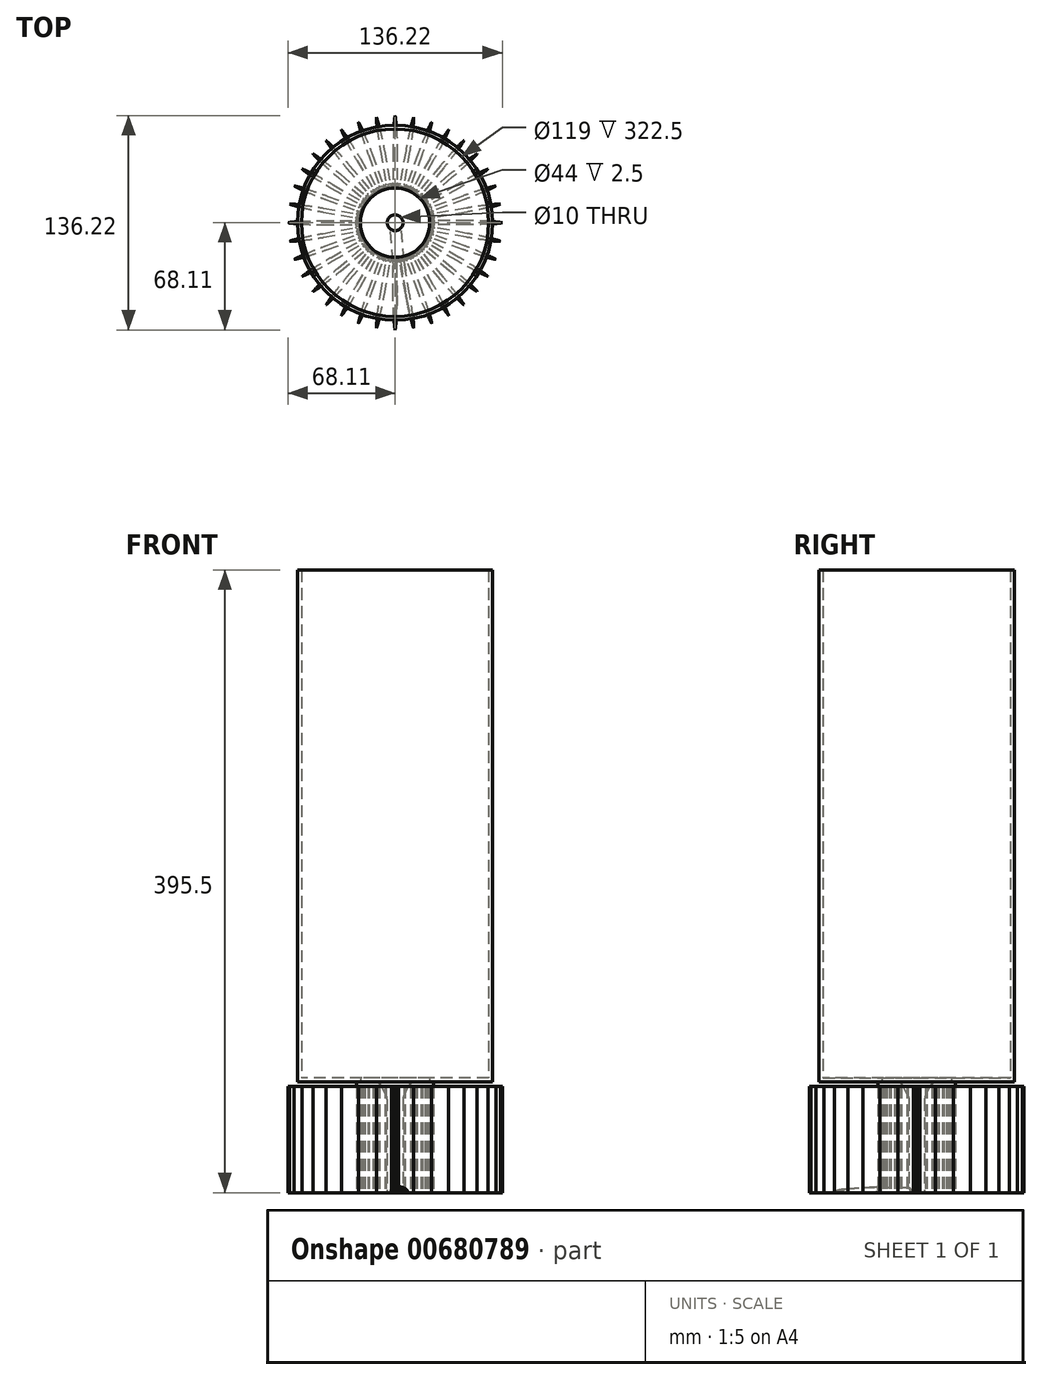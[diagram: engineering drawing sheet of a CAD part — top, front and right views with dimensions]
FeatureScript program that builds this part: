
annotation { "Feature Type Name" : "Feature", "Feature Type Description" : "" }
export const myFeature = defineFeature(function(context is Context, id is Id, definition is map)
    precondition{}
    {
        {
            var Q0;
            Q0=qCreatedBy(makeId("Top.planeOp"),FACE);
            var sketch = newSketch(context, id + "F0", { "sketchPlane" : qUnion([Q0])});
            skCircle(sketch, "E0", {"center": v(0, 0) * mm, "radius": 62 * mm, "construction": true});
            skCircle(sketch, "E1", {"center": v(0, 0) * mm, "radius": 22 * mm, "construction": true});
            skCircle(sketch, "E2", {"center": v(0, 0) * mm, "radius": 24.5 * mm, "construction": true});
            skSolve(sketch);
        }
        {
            var Q0;
            Q0=qCreatedBy(makeId("Top.planeOp"),FACE);
            var sketch = newSketch(context, id + "F1", { "sketchPlane" : qUnion([Q0])});
            skCircle(sketch, "E3", {"center": v(0, 0) * mm, "radius": 24.5 * mm});
            skSolve(sketch);
        }
        {
            var Q0;
            Q0=makeQuery(id+"F1.imprint","IMPRINT",FACE,{"disambiguationData":[TD([[makeQuery(id+"F1.imprint","IMPRINT",EDGE,{"derivedFrom":sQuery(id+"F1.wireOp",EDGE,"E3")}),1.0]])]});
            extrude(context, id + "F2", {"entities" : qUnion([Q0]), "depth" : 70.5 * mm, "offsetDistance" : 25 * mm});
        }
        {
            var Q0;
            Q0=makeQuery(id+"F2.opExtrude","CAP_FACE",FACE,{"disambiguationData":[OSD([sQuery(id+"F1.wireOp",EDGE,"E3")])],"isStart":false});
            var sketch = newSketch(context, id + "F3", { "sketchPlane" : qUnion([Q0])});
            skCircle(sketch, "E4", {"center": v(0, 0) * mm, "radius": 22 * mm});
            skSolve(sketch);
        }
        {
            var Q0;
            Q0=makeQuery(id+"F3.imprint","IMPRINT",FACE,{"disambiguationData":[TD([[makeQuery(id+"F3.imprint","IMPRINT",EDGE,{"derivedFrom":sQuery(id+"F3.wireOp",EDGE,"E4")}),-1.0]])]});
            extrude(context, id + "F4", {"entities" : qUnion([Q0]), "operationType" : NewBodyOperationType.REMOVE, "oppositeDirection" : true, "depth" : 3 * mm, "offsetDistance" : 25 * mm});
        }
        {
            var Q0;
            Q0=qCreatedBy(makeId("Top.planeOp"),FACE);
            var sketch = newSketch(context, id + "F5", { "sketchPlane" : qUnion([Q0])});
            skLineSegment(sketch, "E5", {"start": v(0, 24.5) * mm, "end": v(0, 62) * mm, "construction": true});
            skLineSegment(sketch, "E6.1.0", {"start": v(4.37, 24.1) * mm, "end": v(11.07, 61) * mm, "construction": true});
            skLineSegment(sketch, "E6.2.0", {"start": v(8.6, 22.94) * mm, "end": v(21.79, 58.05) * mm, "construction": true});
            skLineSegment(sketch, "E6.3.0", {"start": v(12.57, 21.03) * mm, "end": v(31.8, 53.22) * mm, "construction": true});
            skLineSegment(sketch, "E6.4.0", {"start": v(16.12, 18.45) * mm, "end": v(40.8, 46.7) * mm, "construction": true});
            skLineSegment(sketch, "E6.5.0", {"start": v(19.15, 15.28) * mm, "end": v(48.47, 38.66) * mm, "construction": true});
            skLineSegment(sketch, "E6.6.0", {"start": v(21.57, 11.6) * mm, "end": v(54.6, 29.38) * mm, "construction": true});
            skLineSegment(sketch, "E6.7.0", {"start": v(23.3, 7.57) * mm, "end": v(58.97, 19.16) * mm, "construction": true});
            skLineSegment(sketch, "E6.8.0", {"start": v(24.28, 3.29) * mm, "end": v(61.44, 8.32) * mm, "construction": true});
            skLineSegment(sketch, "E6.9.0", {"start": v(24.48, -1.1) * mm, "end": v(61.94, -2.78) * mm, "construction": true});
            skLineSegment(sketch, "E6.10.0", {"start": v(23.89, -5.45) * mm, "end": v(60.45, -13.8) * mm, "construction": true});
            skLineSegment(sketch, "E6.11.0", {"start": v(22.53, -9.63) * mm, "end": v(57.01, -24.37) * mm, "construction": true});
            skLineSegment(sketch, "E6.12.0", {"start": v(20.45, -13.5) * mm, "end": v(51.74, -34.16) * mm, "construction": true});
            skLineSegment(sketch, "E6.13.0", {"start": v(17.7, -16.93) * mm, "end": v(44.81, -42.85) * mm, "construction": true});
            skLineSegment(sketch, "E6.14.0", {"start": v(14.4, -19.82) * mm, "end": v(36.44, -50.16) * mm, "construction": true});
            skLineSegment(sketch, "E6.15.0", {"start": v(10.63, -22.07) * mm, "end": v(26.9, -55.86) * mm, "construction": true});
            skLineSegment(sketch, "E6.16.0", {"start": v(6.52, -23.62) * mm, "end": v(16.5, -59.77) * mm, "construction": true});
            skLineSegment(sketch, "E6.17.0", {"start": v(2.2, -24.4) * mm, "end": v(5.56, -61.75) * mm, "construction": true});
            skLineSegment(sketch, "E6.18.0", {"start": v(-2.2, -24.4) * mm, "end": v(-5.56, -61.75) * mm, "construction": true});
            skLineSegment(sketch, "E6.19.0", {"start": v(-6.52, -23.62) * mm, "end": v(-16.5, -59.77) * mm, "construction": true});
            skLineSegment(sketch, "E6.20.0", {"start": v(-10.63, -22.07) * mm, "end": v(-26.9, -55.86) * mm, "construction": true});
            skLineSegment(sketch, "E6.21.0", {"start": v(-14.4, -19.82) * mm, "end": v(-36.44, -50.16) * mm, "construction": true});
            skLineSegment(sketch, "E6.22.0", {"start": v(-17.7, -16.93) * mm, "end": v(-44.81, -42.85) * mm, "construction": true});
            skLineSegment(sketch, "E6.23.0", {"start": v(-20.45, -13.5) * mm, "end": v(-51.74, -34.16) * mm, "construction": true});
            skLineSegment(sketch, "E6.24.0", {"start": v(-22.53, -9.63) * mm, "end": v(-57.01, -24.37) * mm, "construction": true});
            skLineSegment(sketch, "E6.25.0", {"start": v(-23.89, -5.45) * mm, "end": v(-60.45, -13.8) * mm, "construction": true});
            skLineSegment(sketch, "E6.26.0", {"start": v(-24.48, -1.1) * mm, "end": v(-61.94, -2.78) * mm, "construction": true});
            skLineSegment(sketch, "E6.27.0", {"start": v(-24.28, 3.29) * mm, "end": v(-61.44, 8.32) * mm, "construction": true});
            skLineSegment(sketch, "E6.28.0", {"start": v(-23.3, 7.57) * mm, "end": v(-58.97, 19.16) * mm, "construction": true});
            skLineSegment(sketch, "E6.29.0", {"start": v(-21.57, 11.6) * mm, "end": v(-54.6, 29.38) * mm, "construction": true});
            skLineSegment(sketch, "E6.30.0", {"start": v(-19.15, 15.28) * mm, "end": v(-48.47, 38.66) * mm, "construction": true});
            skLineSegment(sketch, "E6.31.0", {"start": v(-16.12, 18.45) * mm, "end": v(-40.8, 46.7) * mm, "construction": true});
            skLineSegment(sketch, "E6.32.0", {"start": v(-12.57, 21.03) * mm, "end": v(-31.8, 53.22) * mm, "construction": true});
            skLineSegment(sketch, "E6.33.0", {"start": v(-8.6, 22.94) * mm, "end": v(-21.79, 58.05) * mm, "construction": true});
            skLineSegment(sketch, "E6.34.0", {"start": v(-4.37, 24.1) * mm, "end": v(-11.07, 61) * mm, "construction": true});
            skPoint(sketch, "E6.center", {"position": v(0, 0) * mm});
            skLineSegment(sketch, "E6.anchor1", {"start": v(0, 0) * mm, "end": v(0, 24.5) * mm, "construction": true});
            skLineSegment(sketch, "E6.anchor2", {"start": v(0, 0) * mm, "end": v(0, 24.5) * mm, "construction": true});
            skSolve(sketch);
        }
        {
            var Q0;
            Q0=qCreatedBy(makeId("Top.planeOp"),FACE);
            var sketch = newSketch(context, id + "F6", { "sketchPlane" : qUnion([Q0])});
            skLineSegment(sketch, "E7.bottom", {"start": v(-1.24, 68.1) * mm, "end": v(1.24, 68.1) * mm, "construction": true});
            skLineSegment(sketch, "E7.left", {"start": v(-1.24, 68.1) * mm, "end": v(-1.24, 24.47) * mm, "construction": true});
            skPoint(sketch, "E7.middle", {"position": v(0, 46.29) * mm});
            skArc(sketch, "E8", {"start": v(1.24, 24.47) * mm, "mid": v(1.69, 24.44) * mm, "end": v(2.14, 24.4) * mm, "construction": true});
            skArc(sketch, "E9", {"start": v(-1.24, 24.47) * mm, "mid": v(-1.69, 24.44) * mm, "end": v(-2.14, 24.4) * mm, "construction": true});
            skLineSegment(sketch, "E10", {"start": v(-2.14, 24.4) * mm, "end": v(0, 0) * mm, "construction": true});
            skLineSegment(sketch, "E11", {"start": v(0, 0) * mm, "end": v(2.14, 24.4) * mm, "construction": true});
            skArc(sketch, "E12", {"start": v(-2.02, 23.1) * mm, "mid": v(0, 23.2) * mm, "end": v(2.02, 23.1) * mm, "construction": true});
            skFitSpline(sketch, "E13", {"points": [v(0, 68.1) * mm, v(-1.24, 46.29) * mm], "startDerivative": vector(-2.7, -15.81) * mm, "endDerivative": vector(0, -17.84) * mm});
            skFitSpline(sketch, "E14.MirrorCS", {"points": [v(0, 68.1) * mm, v(1.24, 46.29) * mm], "startDerivative": vector(2.7, -15.81) * mm, "endDerivative": vector(0, -17.84) * mm});
            skLineSegment(sketch, "E15", {"start": v(-1.24, 46.29) * mm, "end": v(-1.24, 25.38) * mm});
            skLineSegment(sketch, "E16", {"start": v(2.14, 24.4) * mm, "end": v(2.02, 23.1) * mm});
            skLineSegment(sketch, "E17", {"start": v(-2.14, 24.4) * mm, "end": v(-2.02, 23.1) * mm});
            skArc(sketch, "E18", {"start": v(-2.02, 23.1) * mm, "mid": v(0, 23.2) * mm, "end": v(2.02, 23.1) * mm});
            skLineSegment(sketch, "E19", {"start": v(-2.14, 24.4) * mm, "end": v(-2.14, 24.4) * mm});
            skArc(sketch, "E20", {"start": v(2.14, 24.4) * mm, "mid": v(1.69, 24.44) * mm, "end": v(1.24, 24.47) * mm});
            skPoint(sketch, "E21.visualSharp", {"position": v(-1.24, 24.47) * mm});
            skArc(sketch, "E21.filletArc", {"start": v(-2.14, 24.4) * mm, "mid": v(-1.5, 24.72) * mm, "end": v(-1.24, 25.38) * mm});
            skArc(sketch, "E22.MirrorCS", {"start": v(2.14, 24.4) * mm, "mid": v(1.5, 24.72) * mm, "end": v(1.24, 25.38) * mm});
            skLineSegment(sketch, "E23.MirrorCS", {"start": v(1.24, 68.1) * mm, "end": v(1.24, 24.47) * mm, "construction": true});
            skLineSegment(sketch, "E24", {"start": v(1.24, 46.29) * mm, "end": v(1.24, 25.38) * mm});
            skArc(sketch, "E25.filletArc", {"start": v(0.73, 61.3) * mm, "mid": v(0, 61.98) * mm, "end": v(-0.73, 61.3) * mm});
            skSolve(sketch);
        }
        {
            var Q0;
            Q0 = qSketchRegion(id + "F6", true);
            extrude(context, id + "F7", {"entities" : qUnion([Q0]), "depth" : 67.5 * mm, "offsetDistance" : 25 * mm});
        }
        {
            var Q0;
            Q0=qCreatedBy(makeId("Front.planeOp"),FACE);
            var sketch = newSketch(context, id + "F8", { "sketchPlane" : qUnion([Q0])});
            skLineSegment(sketch, "E26", {"start": v(0, 70.5) * mm, "end": v(0, 0) * mm, "construction": true});
            skSolve(sketch);
        }
        {
            var Q0;
            Q0=makeQuery(id+"F7.opExtrude","SWEPT_BODY",BODY,{"disambiguationData":[OSD([sQuery(id+"F6.wireOp",EDGE,"E13"),sQuery(id+"F6.wireOp",EDGE,"E14.MirrorCS"),sQuery(id+"F6.wireOp",EDGE,"E15"),sQuery(id+"F6.wireOp",EDGE,"E16"),sQuery(id+"F6.wireOp",EDGE,"E17"),sQuery(id+"F6.wireOp",EDGE,"E18"),sQuery(id+"F6.wireOp",EDGE,"E21.filletArc"),sQuery(id+"F6.wireOp",EDGE,"E22.MirrorCS"),sQuery(id+"F6.wireOp",EDGE,"E24")])]});
            var Q1;
            Q1=sQuery(id+"F8.wireOp",EDGE,"E26");
            circularPattern(context, id + "F9", {"entities" : qUnion([Q0]), "axis" : qUnion([Q1]), "angle" : 360 * degree, "instanceCount" : 36, "equalSpace" : true});
        }
        {
            var Q0;
            Q0=makeQuery(id+"F9.opPattern","COPY",FACE,{"derivedFrom":makeQuery(id+"F7.opExtrude","CAP_FACE",FACE,{"disambiguationData":[OSD([sQuery(id+"F6.wireOp",EDGE,"E13"),sQuery(id+"F6.wireOp",EDGE,"E14.MirrorCS"),sQuery(id+"F6.wireOp",EDGE,"E15"),sQuery(id+"F6.wireOp",EDGE,"E16"),sQuery(id+"F6.wireOp",EDGE,"E17"),sQuery(id+"F6.wireOp",EDGE,"E18"),sQuery(id+"F6.wireOp",EDGE,"E21.filletArc"),sQuery(id+"F6.wireOp",EDGE,"E22.MirrorCS"),sQuery(id+"F6.wireOp",EDGE,"E24")])],"isStart":false}),"instanceName":"19"});
            var sketch = newSketch(context, id + "F10", { "sketchPlane" : qUnion([Q0])});
            skCircle(sketch, "E27", {"center": v(0, 0) * mm, "radius": 62 * mm, "construction": true});
            skCircle(sketch, "E28", {"center": v(0, 0) * mm, "radius": 22 * mm});
            skCircle(sketch, "E29", {"center": v(0, 0) * mm, "radius": 24.5 * mm});
            skSolve(sketch);
        }
        {
            var Q0;
            Q0 = qSketchRegion(id + "F10", true);
            extrude(context, id + "F11", {"entities" : qUnion([Q0]), "depth" : 3 * mm, "offsetDistance" : 25 * mm});
        }
        {
            var Q0;
            Q0=makeQuery(id+"F11.opExtrude","CAP_FACE",FACE,{"disambiguationData":[OSD([sQuery(id+"F10.wireOp",EDGE,"E28"),sQuery(id+"F10.wireOp",EDGE,"E29")])],"isStart":false});
            var sketch = newSketch(context, id + "F12", { "sketchPlane" : qUnion([Q0])});
            skCircle(sketch, "E30", {"center": v(0, 0) * mm, "radius": 22 * mm});
            skCircle(sketch, "E31", {"center": v(0, 0) * mm, "radius": 62 * mm});
            skSolve(sketch);
        }
        {
            var Q0;
            Q0 = qSketchRegion(id + "F12", true);
            extrude(context, id + "F13", {"entities" : qUnion([Q0]), "operationType" : NewBodyOperationType.ADD, "depth" : 2.5 * mm, "offsetDistance" : 25 * mm});
        }
        {
            var Q0;
            Q0=makeQuery(id+"F13.opExtrude","CAP_FACE",FACE,{"disambiguationData":[OSD([sQuery(id+"F12.wireOp",EDGE,"E30"),sQuery(id+"F12.wireOp",EDGE,"E31")])],"isStart":false});
            var sketch = newSketch(context, id + "F14", { "sketchPlane" : qUnion([Q0])});
            skCircle(sketch, "E32", {"center": v(0, 0) * mm, "radius": 62 * mm});
            skCircle(sketch, "E33", {"center": v(0, 0) * mm, "radius": 59.5 * mm});
            skSolve(sketch);
        }
        {
            var Q0;
            Q0=makeQuery(id+"F14.imprint","IMPRINT",FACE,{"disambiguationData":[TD([[makeQuery(id+"F14.imprint","IMPRINT",EDGE,{"derivedFrom":sQuery(id+"F14.wireOp",EDGE,"E32")}),1.0]])]});
            extrude(context, id + "F15", {"entities" : qUnion([Q0]), "operationType" : NewBodyOperationType.ADD, "depth" : 25 * mm, "offsetDistance" : 25 * mm});
        }
        {
            var Q0;
            Q0=makeQuery(id+"F15.opExtrude","CAP_FACE",FACE,{"disambiguationData":[OSD([sQuery(id+"F14.wireOp",EDGE,"E32"),sQuery(id+"F14.wireOp",EDGE,"E33")])],"isStart":false});
            extrude(context, id + "F16", {"entities" : qUnion([Q0]), "operationType" : NewBodyOperationType.ADD, "depth" : 297.5 * mm, "offsetDistance" : 25 * mm});
        }
        {
            var Q0;
            Q0=qCreatedBy(makeId("Top.planeOp"),FACE);
            var sketch = newSketch(context, id + "F17", { "sketchPlane" : qUnion([Q0])});
            skCircle(sketch, "E34", {"center": v(0, 0) * mm, "radius": 5 * mm});
            skSolve(sketch);
        }
        {
            var Q0;
            Q0 = qSketchRegion(id + "F17", true);
            extrude(context, id + "F18", {"entities" : qUnion([Q0]), "operationType" : NewBodyOperationType.REMOVE, "endBound" : BoundingType.THROUGH_ALL, "depth" : 25 * mm, "offsetDistance" : 25 * mm});
        }
        {
            var Q0;
            Q0=makeQuery(id+"F18.boolean.opBoolean","INTERSECT",EDGE,{"derivedFrom":[makeQuery(id+"F2.opExtrude","CAP_FACE",FACE,{"disambiguationData":[OSD([sQuery(id+"F1.wireOp",EDGE,"E3")])],"isStart":false}),makeQuery(id+"F18.opExtrude","SWEPT_FACE",FACE,{"disambiguationData":[OSD([sQuery(id+"F17.wireOp",EDGE,"E34")])]})]});
            chamfer(context, id + "F19", {"entities" : qUnion([Q0]), "chamferType" : ChamferType.TWO_OFFSETS, "width1" : 5 * mm, "oppositeDirection" : false, "width2" : 10 * mm, "tangentPropagation" : true});
        }
        {
            var Q0;
            {var subQ0=makeQuery(id+"F2.opExtrude","CAP_FACE",FACE,{"disambiguationData":[OSD([sQuery(id+"F1.wireOp",EDGE,"E3")])],"isStart":false});Q0=makeQuery(id+"F19.opChamfer","BLEND_EDGE",EDGE,{"blendedFrom":[makeQuery(id+"F18.boolean.opBoolean","INTERSECT",EDGE,{"derivedFrom":[subQ0,makeQuery(id+"F18.opExtrude","SWEPT_FACE",FACE,{"disambiguationData":[OSD([sQuery(id+"F17.wireOp",EDGE,"E34")])]})]}),subQ0],"blendedInto":[subQ0]});}
            fillet(context, id + "F20", {"entities" : qUnion([Q0]), "radius" : 5 * mm, "tangentPropagation" : true, "allowEdgeOverflow" : false});
        }
        {
            var Q0;
            {var subQ0=makeQuery(id+"F18.opExtrude","SWEPT_FACE",FACE,{"disambiguationData":[OSD([sQuery(id+"F17.wireOp",EDGE,"E34")])]});Q0=makeQuery(id+"F19.opChamfer","BLEND_EDGE",EDGE,{"blendedFrom":[makeQuery(id+"F18.boolean.opBoolean","INTERSECT",EDGE,{"derivedFrom":[makeQuery(id+"F2.opExtrude","CAP_FACE",FACE,{"disambiguationData":[OSD([sQuery(id+"F1.wireOp",EDGE,"E3")])],"isStart":false}),subQ0]}),makeQuery(id+"F18.boolean.opBoolean","COPY",FACE,{"derivedFrom":subQ0})],"blendedInto":[makeQuery(id+"F18.boolean.opBoolean","COPY",FACE,{"derivedFrom":subQ0})]});}
            fillet(context, id + "F21", {"entities" : qUnion([Q0]), "radius" : 5 * mm, "tangentPropagation" : true, "allowEdgeOverflow" : false});
        }
        {
            var Q0;
            Q0=qCreatedBy(makeId("Front.planeOp"),FACE);
            cPlane(context, id + "F22", {"entities" : qUnion([Q0]), "cplaneType" : CPlaneType.OFFSET, "offset" : 62 * mm, "width" : 150 * mm, "height" : 150 * mm});
        }
        {
            var Q0;
            Q0=qCreatedBy(id+"F22.planeOp",FACE);
            var Q1;
            Q1 = qBodyType(qCreatedBy(id + "F8" ,EDGE), BodyType.WIRE);
            cPlane(context, id + "F23", {"entities" : qUnion([Q0, Q1]), "cplaneType" : CPlaneType.LINE_ANGLE, "offset" : 25 * mm, "angle" : 5 * degree, "oppositeDirection" : true, "width" : 150 * mm, "height" : 150 * mm});
        }
        {
            var Q0;
            Q0=qCreatedBy(id+"F23.planeOp",FACE);
            var sketch = newSketch(context, id + "F24", { "sketchPlane" : qUnion([Q0])});
            skLineSegment(sketch, "E35", {"start": v(0, 0) * mm, "end": v(-3.5, 0) * mm});
            skArc(sketch, "E36", {"start": v(-3.5, 0) * mm, "mid": v(-2.47, 2.47) * mm, "end": v(0, 3.5) * mm});
            skArc(sketch, "E37.MirrorCS", {"start": v(3.5, 0) * mm, "mid": v(2.47, 2.47) * mm, "end": v(0, 3.5) * mm});
            skLineSegment(sketch, "E38.MirrorCS", {"start": v(0, 0) * mm, "end": v(3.5, 0) * mm});
            skSolve(sketch);
        }
        {
            var Q0;
            Q0 = qSketchRegion(id + "F24", true);
            extrude(context, id + "F25", {"entities" : qUnion([Q0]), "operationType" : NewBodyOperationType.REMOVE, "endBound" : BoundingType.THROUGH_ALL, "oppositeDirection" : true, "depth" : 25 * mm, "offsetDistance" : 25 * mm});
        }
        {
            var Q0;
            {var subQ0=sQuery(id+"F6.wireOp",EDGE,"E13");var subQ1=sQuery(id+"F6.wireOp",EDGE,"E24");var subQ2=makeQuery(id+"F9.opPattern","COPY",FACE,{"derivedFrom":makeQuery(id+"F7.opExtrude","CAP_FACE",FACE,{"disambiguationData":[OSD([subQ0,sQuery(id+"F6.wireOp",EDGE,"E14.MirrorCS"),sQuery(id+"F6.wireOp",EDGE,"E15"),sQuery(id+"F6.wireOp",EDGE,"E16"),sQuery(id+"F6.wireOp",EDGE,"E17"),sQuery(id+"F6.wireOp",EDGE,"E18"),sQuery(id+"F6.wireOp",EDGE,"E21.filletArc"),sQuery(id+"F6.wireOp",EDGE,"E22.MirrorCS"),subQ1,sQuery(id+"F6.wireOp",EDGE,"E25.filletArc")])],"isStart":true}),"instanceName":"18"});var subQ3=sQuery(id+"F24.wireOp",EDGE,"E37.MirrorCS");var subQ4=makeQuery(id+"F25.opExtrude","SWEPT_FACE",FACE,{"disambiguationData":[OSD([sQuery(id+"F24.wireOp",EDGE,"E36"),subQ3])]});Q0=makeQuery(id+"F25.boolean.opBoolean","COPY",EDGE,{"disambiguationData":[topologyDisambiguationEdgeConnected([subQ2,subQ4]),TD([makeQuery(id+"F9.opPattern","COPY",FACE,{"derivedFrom":makeQuery(id+"F7.opExtrude","SWEPT_FACE",FACE,{"disambiguationData":[OSD([subQ0])]}),"instanceName":"18"})])],"derivedFrom":makeQuery(id+"F25.opExtrude","SWEPT_EDGE",EDGE,{"disambiguationData":[OSD([subQ3,sQuery(id+"F24.wireOp",EDGE,"E38.MirrorCS")])]})});}
            var Q1;
            {var subQ0=sQuery(id+"F6.wireOp",EDGE,"E15");var subQ1=sQuery(id+"F6.wireOp",EDGE,"E14.MirrorCS");var subQ2=makeQuery(id+"F9.opPattern","COPY",FACE,{"derivedFrom":makeQuery(id+"F7.opExtrude","CAP_FACE",FACE,{"disambiguationData":[OSD([sQuery(id+"F6.wireOp",EDGE,"E13"),subQ1,subQ0,sQuery(id+"F6.wireOp",EDGE,"E16"),sQuery(id+"F6.wireOp",EDGE,"E17"),sQuery(id+"F6.wireOp",EDGE,"E18"),sQuery(id+"F6.wireOp",EDGE,"E21.filletArc"),sQuery(id+"F6.wireOp",EDGE,"E22.MirrorCS"),sQuery(id+"F6.wireOp",EDGE,"E24"),sQuery(id+"F6.wireOp",EDGE,"E25.filletArc")])],"isStart":true}),"instanceName":"17"});var subQ3=sQuery(id+"F24.wireOp",EDGE,"E36");var subQ4=makeQuery(id+"F25.opExtrude","SWEPT_FACE",FACE,{"disambiguationData":[OSD([subQ3,sQuery(id+"F24.wireOp",EDGE,"E37.MirrorCS")])]});Q1=makeQuery(id+"F25.boolean.opBoolean","COPY",EDGE,{"disambiguationData":[topologyDisambiguationEdgeConnected([subQ2,subQ4]),TD([makeQuery(id+"F9.opPattern","COPY",FACE,{"derivedFrom":makeQuery(id+"F7.opExtrude","SWEPT_FACE",FACE,{"disambiguationData":[OSD([subQ1])]}),"instanceName":"17"})])],"derivedFrom":makeQuery(id+"F25.opExtrude","SWEPT_EDGE",EDGE,{"disambiguationData":[OSD([sQuery(id+"F24.wireOp",EDGE,"E35"),subQ3])]})});}
            var Q2;
            Q2=makeQuery(id+"F25.boolean.opBoolean","INTERSECT",EDGE,{"derivedFrom":[makeQuery(id+"F9.opPattern","COPY",FACE,{"derivedFrom":makeQuery(id+"F7.opExtrude","SWEPT_FACE",FACE,{"disambiguationData":[OSD([sQuery(id+"F6.wireOp",EDGE,"E13")])]}),"instanceName":"18"}),makeQuery(id+"F25.opExtrude","SWEPT_FACE",FACE,{"disambiguationData":[OSD([sQuery(id+"F24.wireOp",EDGE,"E36"),sQuery(id+"F24.wireOp",EDGE,"E37.MirrorCS")])]})]});
            var Q3;
            Q3=makeQuery(id+"F25.boolean.opBoolean","INTERSECT",EDGE,{"derivedFrom":[makeQuery(id+"F9.opPattern","COPY",FACE,{"derivedFrom":makeQuery(id+"F7.opExtrude","SWEPT_FACE",FACE,{"disambiguationData":[OSD([sQuery(id+"F6.wireOp",EDGE,"E15")])]}),"instanceName":"18"}),makeQuery(id+"F25.opExtrude","SWEPT_FACE",FACE,{"disambiguationData":[OSD([sQuery(id+"F24.wireOp",EDGE,"E36"),sQuery(id+"F24.wireOp",EDGE,"E37.MirrorCS")])]})]});
            var Q4;
            Q4=makeQuery(id+"F25.boolean.opBoolean","INTERSECT",EDGE,{"derivedFrom":[makeQuery(id+"F9.opPattern","COPY",FACE,{"derivedFrom":makeQuery(id+"F7.opExtrude","SWEPT_FACE",FACE,{"disambiguationData":[OSD([sQuery(id+"F6.wireOp",EDGE,"E14.MirrorCS")])]}),"instanceName":"17"}),makeQuery(id+"F25.opExtrude","SWEPT_FACE",FACE,{"disambiguationData":[OSD([sQuery(id+"F24.wireOp",EDGE,"E36"),sQuery(id+"F24.wireOp",EDGE,"E37.MirrorCS")])]})]});
            var Q5;
            Q5=makeQuery(id+"F25.boolean.opBoolean","INTERSECT",EDGE,{"derivedFrom":[makeQuery(id+"F9.opPattern","COPY",FACE,{"derivedFrom":makeQuery(id+"F7.opExtrude","SWEPT_FACE",FACE,{"disambiguationData":[OSD([sQuery(id+"F6.wireOp",EDGE,"E24")])]}),"instanceName":"17"}),makeQuery(id+"F25.opExtrude","SWEPT_FACE",FACE,{"disambiguationData":[OSD([sQuery(id+"F24.wireOp",EDGE,"E36"),sQuery(id+"F24.wireOp",EDGE,"E37.MirrorCS")])]})]});
            fillet(context, id + "F26", {"entities" : qUnion([Q0, Q1, Q2, Q3, Q4, Q5]), "radius" : 0.5 * mm, "tangentPropagation" : true, "allowEdgeOverflow" : false});
        }
    });
